FCSTD DOCUMENT  (FreeCAD 0.16R6712 (Git))
Label: Taster_3fach
License: All rights reserved
LicenseURL: http://en.wikipedia.org/wiki/All_rights_reserved
objects: Sketcher::SketchObject×1
note: 1 computed .brp shape members not serialized (recipe doc carries the construction recipe); baked Part::Feature solids carry a one-line shape summary decoded from their .brp

FEATURE [Sketcher::SketchObject] Sketch
  sketch-geometry (18):
    g0: LineSegment StartX=5.25709 StartY=65.4752 StartZ=0 EndX=58.8571 EndY=65.4752 EndZ=0
    g1: LineSegment StartX=3.95708 StartY=64.1752 StartZ=0 EndX=3.95708 EndY=46.9752 EndZ=0
    g2: LineSegment StartX=3.95708 StartY=46.9752 StartZ=0 EndX=60.1571 EndY=46.9752 EndZ=0
    g3: LineSegment StartX=60.1571 StartY=46.9752 StartZ=0 EndX=60.1571 EndY=64.1752 EndZ=0
    g4: ArcOfCircle CenterX=5.25708 CenterY=64.1752 CenterZ=0 NormalX=0 NormalY=0 NormalZ=1 Radius=1.3 StartAngle=1.57079 EndAngle=3.14159
    g5: ArcOfCircle CenterX=58.8571 CenterY=64.1752 CenterZ=0 NormalX=0 NormalY=0 NormalZ=1 Radius=1.3 StartAngle=6.28319 EndAngle=7.85399
    g6: LineSegment StartX=3.95708 StartY=43.4752 StartZ=0 EndX=60.1571 EndY=43.4752 EndZ=0
    g7: LineSegment StartX=60.1571 StartY=43.4752 StartZ=0 EndX=60.1571 EndY=24.9752 EndZ=0
    g8: LineSegment StartX=60.1571 StartY=24.9752 StartZ=0 EndX=3.95708 EndY=24.9752 EndZ=0
    g9: LineSegment StartX=3.95708 StartY=24.9752 StartZ=0 EndX=3.95708 EndY=43.4752 EndZ=0
    g10: LineSegment StartX=3.95708 StartY=21.4752 StartZ=0 EndX=3.95708 EndY=4.27516 EndZ=0
    g11: LineSegment StartX=3.95708 StartY=21.4752 StartZ=0 EndX=60.1571 EndY=21.4752 EndZ=0
    g12: LineSegment StartX=60.1571 StartY=21.4752 StartZ=0 EndX=60.1571 EndY=4.27516 EndZ=0
    g13: LineSegment StartX=5.25708 StartY=2.97516 StartZ=0 EndX=58.8571 EndY=2.97516 EndZ=0
    g14: ArcOfCircle CenterX=5.25708 CenterY=4.27516 CenterZ=0 NormalX=0 NormalY=0 NormalZ=1 Radius=1.3 StartAngle=3.14159 EndAngle=4.71239
    g15: ArcOfCircle CenterX=58.8571 CenterY=4.27516 CenterZ=0 NormalX=0 NormalY=0 NormalZ=1 Radius=1.3 StartAngle=4.71238 EndAngle=6.28319
    g16: LineSegment [constr] StartX=60.1571 StartY=46.9752 StartZ=0 EndX=60.1571 EndY=43.4752 EndZ=0
    g17: LineSegment [constr] StartX=60.1571 StartY=24.9752 StartZ=0 EndX=60.1571 EndY=21.4752 EndZ=0
  constraints (55):
    c: Horizontal(g0)
    c: Vertical(g1)
    c: Coincident(g2,g1)
    c: Horizontal(g2)
    c: Vertical(g3)
    c: Coincident(g2,g3)
    c: Coincident(g4,g0)
    c: Coincident(g4,g1)
    c: Coincident(g5,g0)
    c: Coincident(g5,g3)
    c: Tangent(g4,g1)
    c: Tangent(g4,g0)
    c: Tangent(g0,g5)
    c: Tangent(g5,g3)
    c: DistanceX(g2,g2) = 56.2
    c: DistanceY(g2,g0) = 18.5
    c: Radius(g5) = 1.3
    c: Equal(g4,g5)
    c: Coincident(g6,g7)
    c: Coincident(g7,g8)
    c: Coincident(g8,g9)
    c: Coincident(g9,g6)
    c: Horizontal(g6)
    c: Horizontal(g8)
    c: Vertical(g7)
    c: Vertical(g9)
    c: Vertical(g10)
    c: Coincident(g11,g10)
    c: Horizontal(g11)
    c: Coincident(g12,g11)
    c: Vertical(g12)
    c: Horizontal(g13)
    c: Coincident(g14,g10)
    c: Coincident(g14,g13)
    c: Coincident(g15,g12)
    c: Coincident(g15,g13)
    c: Equal(g2,g6)
    c: Equal(g6,g8)
    c: Equal(g8,g11)
    c: DistanceY(g13,g11) = 18.5
    c: Equal(g5,g15)
    c: Equal(g14,g15)
    c: Tangent(g15,g12)
    c: Tangent(g15,g13)
    c: Tangent(g13,g14)
    c: Tangent(g10,g14)
    c: DistanceY(g7,g7) = 18.5
    c: Coincident(g16,g2)
    c: Coincident(g16,g6)
    c: Vertical(g16)
    c: Coincident(g17,g7)
    c: Vertical(g17)
    c: DistanceY(g16,g16) = 3.5
    c: Coincident(g11,g17)
    c: Equal(g16,g17)
